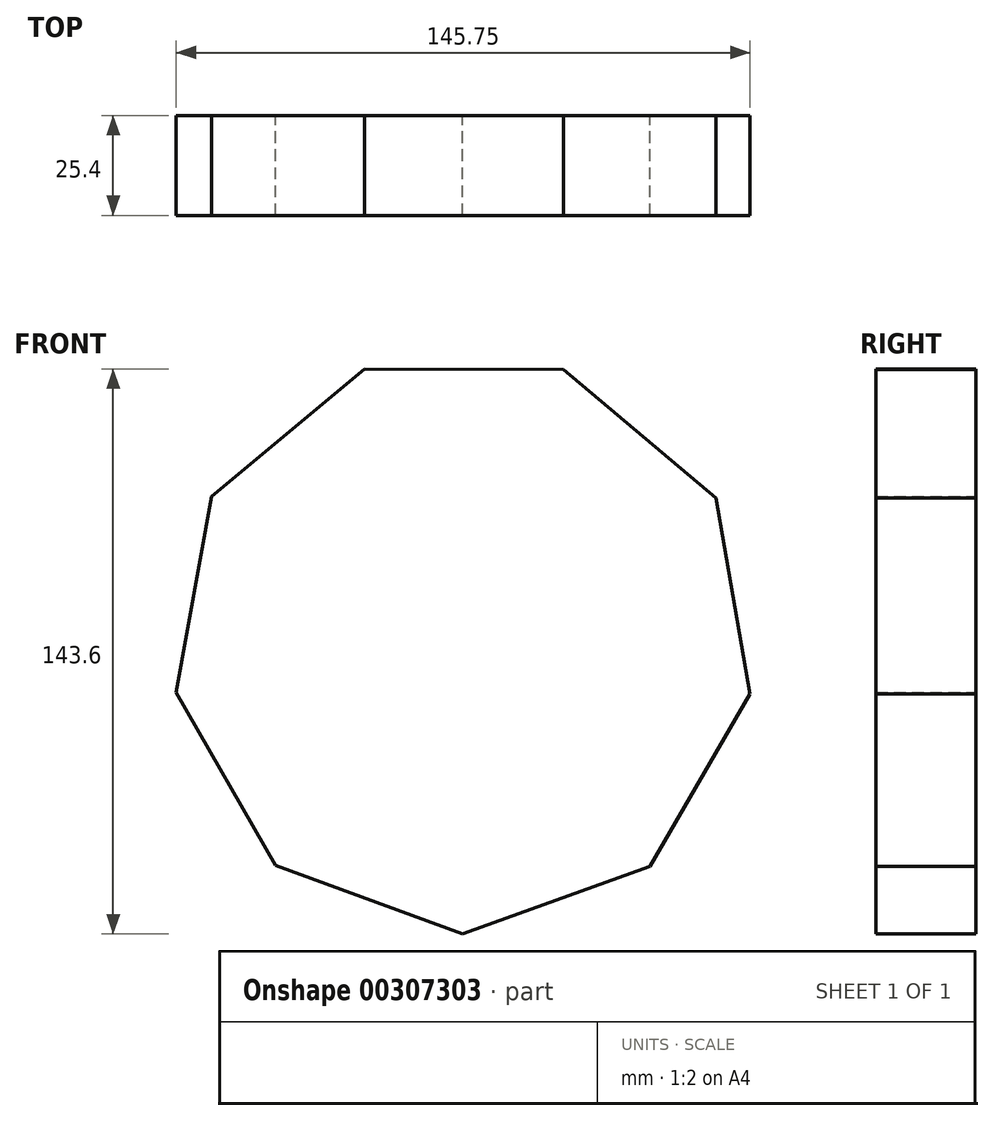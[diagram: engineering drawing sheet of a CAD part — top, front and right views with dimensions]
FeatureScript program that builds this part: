
annotation { "Feature Type Name" : "Feature", "Feature Type Description" : "" }
export const myFeature = defineFeature(function(context is Context, id is Id, definition is map)
    precondition{}
    {
        {
            var Q0;
            Q0=qCreatedBy(makeId("Front.planeOp"),FACE);
            var sketch = newSketch(context, id + "F0", { "sketchPlane" : qUnion([Q0])});
            skCircle(sketch, "E0.cCircle", {"center": v(0, 0) * mm, "radius": 74 * mm, "construction": true});
            skLineSegment(sketch, "E0.0", {"start": v(64.19, 36.83) * mm, "end": v(72.84, -13.05) * mm});
            skLineSegment(sketch, "E0.1", {"start": v(72.84, -13.05) * mm, "end": v(47.41, -56.82) * mm});
            skLineSegment(sketch, "E0.2", {"start": v(47.41, -56.82) * mm, "end": v(-0.2, -74) * mm});
            skLineSegment(sketch, "E0.3", {"start": v(-0.2, -74) * mm, "end": v(-47.72, -56.56) * mm});
            skLineSegment(sketch, "E0.4", {"start": v(-47.72, -56.56) * mm, "end": v(-72.9, -12.65) * mm});
            skLineSegment(sketch, "E0.5", {"start": v(-72.9, -12.65) * mm, "end": v(-63.98, 37.17) * mm});
            skLineSegment(sketch, "E0.6", {"start": v(-63.98, 37.17) * mm, "end": v(-25.12, 69.6) * mm});
            skLineSegment(sketch, "E0.7", {"start": v(-25.12, 69.6) * mm, "end": v(25.5, 69.47) * mm});
            skLineSegment(sketch, "E0.8", {"start": v(25.5, 69.47) * mm, "end": v(64.19, 36.83) * mm});
            skSolve(sketch);
        }
        {
            var Q0;
            Q0=makeQuery(id+"F0.imprint","IMPRINT",FACE,{"disambiguationData":[TD([[makeQuery(id+"F0.imprint","IMPRINT",EDGE,{"derivedFrom":sQuery(id+"F0.wireOp",EDGE,"E0.0")}),-1.0]])]});
            extrude(context, id + "F1", {"entities" : qUnion([Q0]), "depth" : 25.4 * mm});
        }
    });
